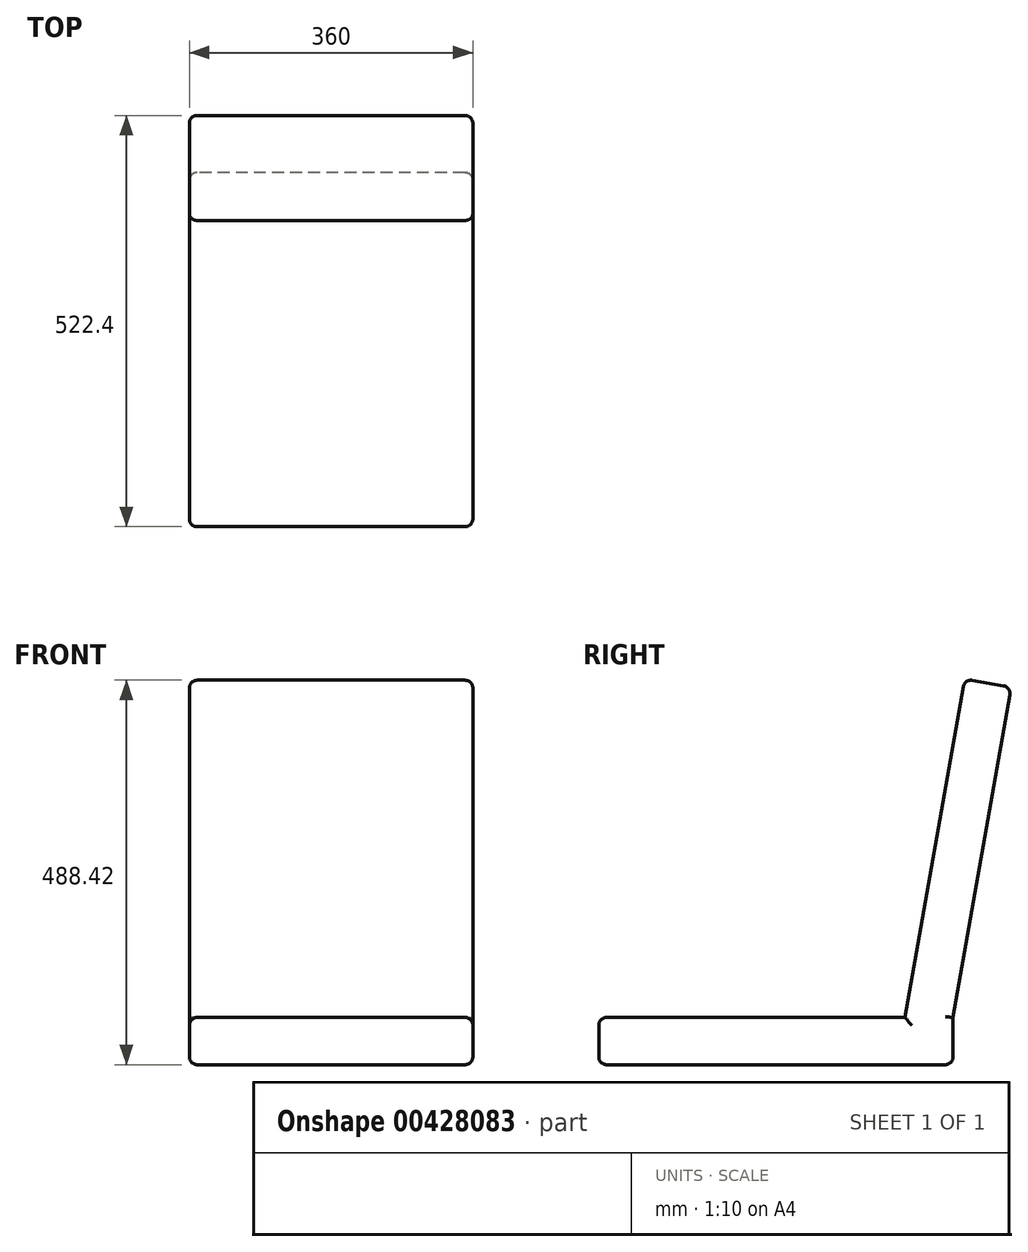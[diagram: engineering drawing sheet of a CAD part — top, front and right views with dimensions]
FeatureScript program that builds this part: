
annotation { "Feature Type Name" : "Feature", "Feature Type Description" : "" }
export const myFeature = defineFeature(function(context is Context, id is Id, definition is map)
    precondition{}
    {
        {
            var Q0;
            Q0=qCreatedBy(makeId("Top.planeOp"),FACE);
            var sketch = newSketch(context, id + "F0", { "sketchPlane" : qUnion([Q0])});
            skLineSegment(sketch, "E0.bottom", {"start": v(180, 225) * mm, "end": v(-180, 225) * mm});
            skLineSegment(sketch, "E0.top", {"start": v(180, -225) * mm, "end": v(-180, -225) * mm});
            skLineSegment(sketch, "E0.left", {"start": v(180, 225) * mm, "end": v(180, -225) * mm});
            skLineSegment(sketch, "E0.right", {"start": v(-180, 225) * mm, "end": v(-180, -225) * mm});
            skPoint(sketch, "E0.middle", {"position": v(0, 0) * mm});
            skSolve(sketch);
        }
        {
            var Q0;
            Q0=makeQuery(id+"F0.imprint","IMPRINT",FACE,{"disambiguationData":[TD([[makeQuery(id+"F0.imprint","IMPRINT",EDGE,{"derivedFrom":sQuery(id+"F0.wireOp",EDGE,"E0.bottom")}),1.0]])]});
            extrude(context, id + "F1", {"entities" : qUnion([Q0]), "depth" : 60 * mm});
        }
        {
            var Q0;
            Q0=makeQuery(id+"F1.opExtrude","SWEPT_FACE",FACE,{"disambiguationData":[OSD([sQuery(id+"F0.wireOp",EDGE,"E0.right")])]});
            var sketch = newSketch(context, id + "F2", { "sketchPlane" : qUnion([Q0])});
            skLineSegment(sketch, "E1", {"start": v(-225, 60) * mm, "end": v(-298.98, 479.58) * mm});
            skLineSegment(sketch, "E2", {"start": v(-298.98, 479.58) * mm, "end": v(-239.9, 490) * mm});
            skLineSegment(sketch, "E3", {"start": v(-239.9, 490) * mm, "end": v(-164.07, 60) * mm});
            skLineSegment(sketch, "E4", {"start": v(-164.07, 60) * mm, "end": v(-225, 60) * mm});
            skPoint(sketch, "E5.0.end.orphan", {"position": v(-225, 0) * mm});
            skSolve(sketch);
        }
        {
            var Q0;
            Q0=makeQuery(id+"F2.imprint","IMPRINT",FACE,{"disambiguationData":[TD([[makeQuery(id+"F2.imprint","IMPRINT",EDGE,{"derivedFrom":sQuery(id+"F2.wireOp",EDGE,"E1")}),-1.0]])]});
            var Q1;
            Q1=makeQuery(id+"F1.opExtrude","SWEPT_FACE",FACE,{"disambiguationData":[OSD([sQuery(id+"F0.wireOp",EDGE,"E0.left")])]});
            extrude(context, id + "F3", {"entities" : qUnion([Q0]), "operationType" : NewBodyOperationType.ADD, "endBound" : BoundingType.UP_TO_SURFACE, "oppositeDirection" : true, "endBoundEntityFace" : qUnion([Q1]), "depth" : 25 * mm});
        }
        {
            var Q0;
            Q0=makeQuery(id+"F3.boolean.opBoolean","MERGE",FACE,{"derivedFrom":[makeQuery(id+"F1.opExtrude","SWEPT_FACE",FACE,{"disambiguationData":[OSD([sQuery(id+"F0.wireOp",EDGE,"E0.right")])]}),makeQuery(id+"F3.opExtrude","CAP_FACE",FACE,{"disambiguationData":[OSD([sQuery(id+"F2.wireOp",EDGE,"E1"),sQuery(id+"F2.wireOp",EDGE,"E2"),sQuery(id+"F2.wireOp",EDGE,"E3"),sQuery(id+"F2.wireOp",EDGE,"E4")])],"isStart":true})]});
            var Q1;
            {var subQ0=sQuery(id+"F0.wireOp",EDGE,"E0.left");Q1=makeQuery(id+"F3.boolean.opBoolean","MERGE",FACE,{"derivedFrom":[makeQuery(id+"F1.opExtrude","SWEPT_FACE",FACE,{"disambiguationData":[OSD([subQ0])]}),makeQuery(id+"F3.opExtrude","CAP_FACE",FACE,{"disambiguationData":[OSD([subQ0])],"isStart":false})]});}
            var Q2;
            Q2=makeQuery(id+"F1.opExtrude","SWEPT_FACE",FACE,{"disambiguationData":[OSD([sQuery(id+"F0.wireOp",EDGE,"E0.top")])]});
            var Q3;
            Q3=makeQuery(id+"F3.opExtrude","SWEPT_FACE",FACE,{"disambiguationData":[OSD([sQuery(id+"F2.wireOp",EDGE,"E2")])]});
            var Q4;
            Q4=makeQuery(id+"F1.opExtrude","CAP_FACE",FACE,{"disambiguationData":[OSD([sQuery(id+"F0.wireOp",EDGE,"E0.bottom"),sQuery(id+"F0.wireOp",EDGE,"E0.top"),sQuery(id+"F0.wireOp",EDGE,"E0.left"),sQuery(id+"F0.wireOp",EDGE,"E0.right")])],"isStart":true});
            fillet(context, id + "F4", {"entities" : qUnion([Q0, Q1, Q2, Q3, Q4]), "radius" : 10 * mm, "tangentPropagation" : true, "allowEdgeOverflow" : false});
        }
    });
